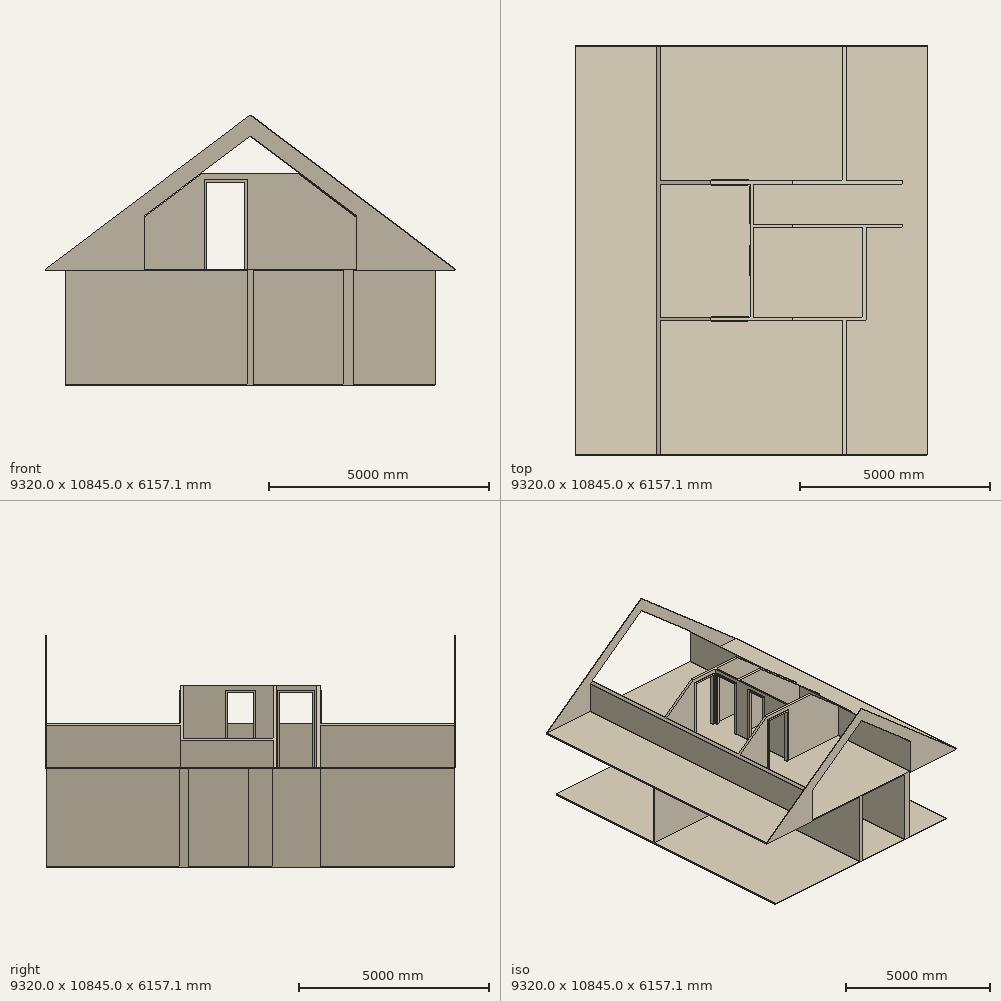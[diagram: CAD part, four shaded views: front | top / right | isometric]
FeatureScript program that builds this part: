
annotation { "Feature Type Name" : "Feature", "Feature Type Description" : "" }
export const myFeature = defineFeature(function(context is Context, id is Id, definition is map)
    precondition{}
    {
        {
            var Q0;
            Q0=qCreatedBy(makeId("Top.planeOp"),FACE);
            cPlane(context, id + "F0", {"entities" : qUnion([Q0]), "cplaneType" : CPlaneType.OFFSET, "offset" : 0 * mm, "width" : 150 * mm, "height" : 150 * mm});
        }
        {
            var Q0;
            Q0=qCreatedBy(makeId("Top.planeOp"),FACE);
            cPlane(context, id + "F1", {"entities" : qUnion([Q0]), "cplaneType" : CPlaneType.OFFSET, "offset" : 2600 * mm, "width" : 150 * mm, "height" : 150 * mm});
        }
        {
            var Q0;
            Q0=qCreatedBy(id+"F0.planeOp",FACE);
            var sketch = newSketch(context, id + "F2", { "sketchPlane" : qUnion([Q0])});
            skLineSegment(sketch, "E0.bottom", {"start": v(-4200, 0) * mm, "end": v(4200, 0) * mm});
            skLineSegment(sketch, "E0.top", {"start": v(-4200, 10795) * mm, "end": v(4200, 10795) * mm});
            skLineSegment(sketch, "E0.left", {"start": v(-4200, 10795) * mm, "end": v(-4200, 0) * mm});
            skLineSegment(sketch, "E0.right", {"start": v(4200, 10795) * mm, "end": v(4200, 0) * mm});
            skSolve(sketch);
        }
        {
            var Q0;
            Q0 = qSketchRegion(id + "F2", true);
            extrude(context, id + "F3", {"entities" : qUnion([Q0]), "oppositeDirection" : true, "depth" : 25 * mm, "offsetDistance" : 25 * mm});
        }
        {
            var Q0;
            Q0=makeQuery(id+"F3.opExtrude","CAP_FACE",FACE,{"disambiguationData":[OSD([sQuery(id+"F2.wireOp",EDGE,"E0.bottom"),sQuery(id+"F2.wireOp",EDGE,"E0.top"),sQuery(id+"F2.wireOp",EDGE,"E0.left"),sQuery(id+"F2.wireOp",EDGE,"E0.right")])],"isStart":true});
            var sketch = newSketch(context, id + "F4", { "sketchPlane" : qUnion([Q0])});
            skLineSegment(sketch, "E1", {"start": v(-66, 0) * mm, "end": v(-66, 5971.5) * mm});
            skLineSegment(sketch, "E2", {"start": v(-66, 0) * mm, "end": v(66, 0) * mm});
            skLineSegment(sketch, "E3", {"start": v(66, 0) * mm, "end": v(66, 3518.5) * mm});
            skLineSegment(sketch, "E4", {"start": v(2119, 0) * mm, "end": v(2349, 0) * mm});
            skLineSegment(sketch, "E5", {"start": v(2349, 0) * mm, "end": v(2349, 3518.5) * mm});
            skLineSegment(sketch, "E6", {"start": v(1066, 7175) * mm, "end": v(1066, 5975) * mm});
            skLineSegment(sketch, "E7", {"start": v(1066, 5975) * mm, "end": v(2900, 5975) * mm});
            skLineSegment(sketch, "E8", {"start": v(2900, 5975) * mm, "end": v(2900, 5355) * mm});
            skLineSegment(sketch, "E9", {"start": v(2900, 5355) * mm, "end": v(3000, 5355) * mm});
            skLineSegment(sketch, "E10", {"start": v(3000, 5355) * mm, "end": v(3000, 5975) * mm});
            skLineSegment(sketch, "E11", {"start": v(3000, 5975) * mm, "end": v(4200, 5975) * mm});
            skLineSegment(sketch, "E12", {"start": v(-66, 5971.5) * mm, "end": v(-4200, 5971.5) * mm});
            skLineSegment(sketch, "E13", {"start": v(-4200, 5971.5) * mm, "end": v(-4200, 6028.5) * mm});
            skLineSegment(sketch, "E14", {"start": v(-4200, 6028.5) * mm, "end": v(-66, 6028.5) * mm});
            skLineSegment(sketch, "E15", {"start": v(-66, 6028.5) * mm, "end": v(-66, 10800) * mm});
            skLineSegment(sketch, "E16", {"start": v(-66, 10800) * mm, "end": v(66, 10800) * mm});
            skLineSegment(sketch, "E17", {"start": v(2119, 0) * mm, "end": v(2119, 3518.5) * mm});
            skLineSegment(sketch, "E18", {"start": v(2119, 3518.5) * mm, "end": v(66, 3518.5) * mm});
            skLineSegment(sketch, "E19", {"start": v(2349, 3518.5) * mm, "end": v(4200, 3518.5) * mm});
            skLineSegment(sketch, "E20", {"start": v(4200, 3518.5) * mm, "end": v(4200, 3748.5) * mm});
            skLineSegment(sketch, "E21", {"start": v(4200, 3748.5) * mm, "end": v(66, 3748.5) * mm});
            skPoint(sketch, "E22", {"position": v(2234, 0) * mm});
            skPoint(sketch, "E23", {"position": v(4200, 3633.5) * mm});
            skPoint(sketch, "E24", {"position": v(-4200, 6000) * mm});
            skLineSegment(sketch, "E25", {"start": v(66, 3748.5) * mm, "end": v(66, 7175) * mm});
            skLineSegment(sketch, "E26", {"start": v(66, 10800) * mm, "end": v(66, 7242) * mm});
            skLineSegment(sketch, "E27", {"start": v(66, 7175) * mm, "end": v(1066, 7175) * mm});
            skLineSegment(sketch, "E28", {"start": v(66, 7242) * mm, "end": v(4200, 7242) * mm});
            skLineSegment(sketch, "E29", {"start": v(4200, 7242) * mm, "end": v(4200, 5975) * mm});
            skSolve(sketch);
        }
        {
            var Q0;
            Q0 = qSketchRegion(id + "F4", true);
            var Q1;
            Q1=qCreatedBy(id+"F1.planeOp",FACE);
            extrude(context, id + "F5", {"entities" : qUnion([Q0]), "operationType" : NewBodyOperationType.ADD, "endBound" : BoundingType.UP_TO_SURFACE, "depth" : 25 * mm, "endBoundEntityFace" : qUnion([Q1]), "offsetDistance" : 25 * mm});
        }
        {
            var Q0;
            Q0=qCreatedBy(id+"F1.planeOp",FACE);
            var sketch = newSketch(context, id + "F6", { "sketchPlane" : qUnion([Q0])});
            skLineSegment(sketch, "E30.bottom", {"start": v(-4660, 10795) * mm, "end": v(4660, 10795) * mm});
            skLineSegment(sketch, "E30.top", {"start": v(-4660, 0) * mm, "end": v(4660, 0) * mm});
            skLineSegment(sketch, "E30.left", {"start": v(-4660, 10795) * mm, "end": v(-4660, 0) * mm});
            skLineSegment(sketch, "E30.right", {"start": v(4660, 10795) * mm, "end": v(4660, 0) * mm});
            skSolve(sketch);
        }
        {
            var Q0;
            Q0 = qSketchRegion(id + "F6", true);
            extrude(context, id + "F7", {"entities" : qUnion([Q0]), "operationType" : NewBodyOperationType.ADD, "depth" : 25 * mm, "offsetDistance" : 25 * mm});
        }
        {
            var Q0;
            Q0=makeQuery(id+"F7.opExtrude","SWEPT_FACE",FACE,{"disambiguationData":[OSD([sQuery(id+"F6.wireOp",EDGE,"E30.bottom")])]});
            var sketch = newSketch(context, id + "F8", { "sketchPlane" : qUnion([Q0])});
            skLineSegment(sketch, "E31.top", {"start": v(-2415, 3833.53) * mm, "end": v(0, 5653.36) * mm});
            skLineSegment(sketch, "E31.left", {"start": v(-2415, 2600) * mm, "end": v(-2415, 3833.53) * mm});
            skLineSegment(sketch, "E32", {"start": v(-2415, 2600) * mm, "end": v(-4658.15, 2600) * mm});
            skLineSegment(sketch, "E33", {"start": v(-4658.15, 2600) * mm, "end": v(-4658.15, 2621.92) * mm});
            skLineSegment(sketch, "E34", {"start": v(-4658.15, 2621.92) * mm, "end": v(0, 6132.09) * mm});
            skLineSegment(sketch, "E35", {"start": v(0, 6132.09) * mm, "end": v(4658.15, 2621.92) * mm});
            skLineSegment(sketch, "E36", {"start": v(4658.15, 2621.92) * mm, "end": v(4658.15, 2600) * mm});
            skLineSegment(sketch, "E37", {"start": v(4658.15, 2600) * mm, "end": v(2415, 2600) * mm});
            skLineSegment(sketch, "E38", {"start": v(2415, 2600) * mm, "end": v(2415, 3833.53) * mm});
            skLineSegment(sketch, "E39", {"start": v(2415, 3833.53) * mm, "end": v(0, 5653.36) * mm});
            skSolve(sketch);
        }
        {
            var Q0;
            Q0 = qSketchRegion(id + "F8", true);
            extrude(context, id + "F9", {"entities" : qUnion([Q0]), "operationType" : NewBodyOperationType.ADD, "depth" : 25 * mm, "offsetDistance" : 25 * mm});
        }
        {
            var Q0;
            Q0=qCreatedBy(id+"F1.planeOp",FACE);
            var sketch = newSketch(context, id + "F10", { "sketchPlane" : qUnion([Q0])});
            skLineSegment(sketch, "E40", {"start": v(-2510, 10795) * mm, "end": v(-2510, 0) * mm});
            skLineSegment(sketch, "E41", {"start": v(-2510, 0) * mm, "end": v(-2415, 0) * mm});
            skLineSegment(sketch, "E42", {"start": v(-2415, 0) * mm, "end": v(-2415, 3535) * mm});
            skLineSegment(sketch, "E43", {"start": v(-2415, 3535) * mm, "end": v(2415, 3535) * mm});
            skLineSegment(sketch, "E44", {"start": v(2415, 3535) * mm, "end": v(2415, 0) * mm});
            skLineSegment(sketch, "E45", {"start": v(2415, 0) * mm, "end": v(2510, 0) * mm});
            skLineSegment(sketch, "E46", {"start": v(2510, 0) * mm, "end": v(2510, 3535) * mm});
            skLineSegment(sketch, "E47", {"start": v(2510, 3535) * mm, "end": v(3035, 3535) * mm});
            skLineSegment(sketch, "E48", {"start": v(3035, 3535) * mm, "end": v(3035, 5995) * mm});
            skLineSegment(sketch, "E49", {"start": v(3035, 5995) * mm, "end": v(4660, 5995) * mm});
            skLineSegment(sketch, "E50", {"start": v(4660, 5995) * mm, "end": v(4660, 6090) * mm});
            skLineSegment(sketch, "E51", {"start": v(4660, 6090) * mm, "end": v(40, 6090) * mm});
            skLineSegment(sketch, "E52", {"start": v(40, 6090) * mm, "end": v(40, 7150) * mm});
            skLineSegment(sketch, "E53", {"start": v(40, 7150) * mm, "end": v(4660, 7150) * mm});
            skLineSegment(sketch, "E54", {"start": v(4660, 7150) * mm, "end": v(4660, 7245) * mm});
            skLineSegment(sketch, "E55", {"start": v(4660, 7245) * mm, "end": v(2510, 7245) * mm});
            skLineSegment(sketch, "E56", {"start": v(2510, 7245) * mm, "end": v(2510, 10795) * mm});
            skLineSegment(sketch, "E57", {"start": v(2510, 10795) * mm, "end": v(2415, 10795) * mm});
            skLineSegment(sketch, "E58", {"start": v(2415, 10795) * mm, "end": v(2415, 7245) * mm});
            skLineSegment(sketch, "E59", {"start": v(2415, 7245) * mm, "end": v(-2415, 7245) * mm});
            skLineSegment(sketch, "E60", {"start": v(-2415, 7245) * mm, "end": v(-2415, 10795) * mm});
            skLineSegment(sketch, "E61", {"start": v(-2415, 10795) * mm, "end": v(-2510, 10795) * mm});
            skLineSegment(sketch, "E62.bottom", {"start": v(-2415, 7150) * mm, "end": v(-15, 7150) * mm});
            skLineSegment(sketch, "E62.top", {"start": v(-2415, 3630) * mm, "end": v(-15, 3630) * mm});
            skLineSegment(sketch, "E62.left", {"start": v(-2415, 7150) * mm, "end": v(-2415, 3630) * mm});
            skLineSegment(sketch, "E62.right", {"start": v(-15, 7150) * mm, "end": v(-15, 3630) * mm});
            skLineSegment(sketch, "E63.bottom", {"start": v(40, 5995) * mm, "end": v(2940, 5995) * mm});
            skLineSegment(sketch, "E63.top", {"start": v(40, 3630) * mm, "end": v(2940, 3630) * mm});
            skLineSegment(sketch, "E63.left", {"start": v(40, 5995) * mm, "end": v(40, 3630) * mm});
            skLineSegment(sketch, "E63.right", {"start": v(2940, 5995) * mm, "end": v(2940, 3630) * mm});
            skSolve(sketch);
        }
        {
            var Q0;
            Q0 = qSketchRegion(id + "F10", true);
            extrude(context, id + "F11", {"entities" : qUnion([Q0]), "operationType" : NewBodyOperationType.ADD, "depth" : 2200 * mm, "offsetDistance" : 25 * mm});
        }
        {
            var Q0;
            Q0=makeQuery(id+"F11.boolean.opBoolean","MERGE",FACE,{"derivedFrom":[makeQuery(id+"F7.opExtrude","SWEPT_FACE",FACE,{"disambiguationData":[OSD([sQuery(id+"F6.wireOp",EDGE,"E30.top")])]}),makeQuery(id+"F11.opExtrude","SWEPT_FACE",FACE,{"disambiguationData":[OSD([sQuery(id+"F10.wireOp",EDGE,"E41")])]}),makeQuery(id+"F11.opExtrude","SWEPT_FACE",FACE,{"disambiguationData":[OSD([sQuery(id+"F10.wireOp",EDGE,"E45")])]})]});
            var sketch = newSketch(context, id + "F12", { "sketchPlane" : qUnion([Q0])});
            skLineSegment(sketch, "E64.top", {"start": v(-2415, 3833.53) * mm, "end": v(0, 5653.36) * mm});
            skLineSegment(sketch, "E64.left", {"start": v(-2415, 2600) * mm, "end": v(-2415, 3833.53) * mm});
            skLineSegment(sketch, "E65", {"start": v(-2415, 2600) * mm, "end": v(-4658.15, 2600) * mm});
            skLineSegment(sketch, "E66", {"start": v(-4658.15, 2600) * mm, "end": v(-4658.15, 2621.92) * mm});
            skLineSegment(sketch, "E67", {"start": v(-4658.15, 2621.92) * mm, "end": v(0, 6132.09) * mm});
            skLineSegment(sketch, "E68", {"start": v(0, 6132.09) * mm, "end": v(4658.15, 2621.92) * mm});
            skLineSegment(sketch, "E69", {"start": v(4658.15, 2621.92) * mm, "end": v(4658.15, 2600) * mm});
            skLineSegment(sketch, "E70", {"start": v(4658.15, 2600) * mm, "end": v(2415, 2600) * mm});
            skLineSegment(sketch, "E71", {"start": v(2415, 2600) * mm, "end": v(2415, 3833.53) * mm});
            skLineSegment(sketch, "E72", {"start": v(2415, 3833.53) * mm, "end": v(0, 5653.36) * mm});
            skSolve(sketch);
        }
        {
            var Q0;
            Q0 = qSketchRegion(id + "F12", true);
            extrude(context, id + "F13", {"entities" : qUnion([Q0]), "operationType" : NewBodyOperationType.ADD, "depth" : 25 * mm, "offsetDistance" : 25 * mm});
        }
        {
            var Q0;
            Q0=makeQuery(id+"F11.opExtrude","SWEPT_FACE",FACE,{"disambiguationData":[OSD([sQuery(id+"F10.wireOp",EDGE,"E57")])]});
            var sketch = newSketch(context, id + "F14", { "sketchPlane" : qUnion([Q0])});
            skLineSegment(sketch, "E73", {"start": v(-4660, 4800) * mm, "end": v(-4660, 2625) * mm});
            skLineSegment(sketch, "E74", {"start": v(-3980.91, 2625) * mm, "end": v(-2415, 3805) * mm});
            skLineSegment(sketch, "E75", {"start": v(-1094.6, 4800) * mm, "end": v(-4660, 4800) * mm});
            skLineSegment(sketch, "E76", {"start": v(1094.6, 4800) * mm, "end": v(4660, 4800) * mm});
            skLineSegment(sketch, "E77", {"start": v(-4660, 2625) * mm, "end": v(-3980.91, 2625) * mm});
            skLineSegment(sketch, "E78", {"start": v(2415, 3805) * mm, "end": v(3980.91, 2625) * mm});
            skLineSegment(sketch, "E79", {"start": v(4660, 2625) * mm, "end": v(4660, 4800) * mm});
            skLineSegment(sketch, "E80", {"start": v(4660, 2625) * mm, "end": v(3980.91, 2625) * mm});
            skLineSegment(sketch, "E81", {"start": v(2415, 3805) * mm, "end": v(1094.6, 4800) * mm});
            skLineSegment(sketch, "E82", {"start": v(-2415, 3805) * mm, "end": v(-1094.6, 4800) * mm});
            skSolve(sketch);
        }
        {
            var Q0;
            Q0 = qSketchRegion(id + "F14", true);
            extrude(context, id + "F15", {"entities" : qUnion([Q0]), "operationType" : NewBodyOperationType.REMOVE, "oppositeDirection" : true, "depth" : 10795 * mm, "offsetDistance" : 25 * mm});
        }
        {
            var Q0;
            Q0=makeQuery(id+"F11.opExtrude","SWEPT_FACE",FACE,{"disambiguationData":[OSD([sQuery(id+"F10.wireOp",EDGE,"E59")])]});
            var sketch = newSketch(context, id + "F16", { "sketchPlane" : qUnion([Q0])});
            skLineSegment(sketch, "E83.bottom", {"start": v(135, 4605) * mm, "end": v(995, 4605) * mm});
            skLineSegment(sketch, "E83.top", {"start": v(135, 2625) * mm, "end": v(995, 2625) * mm});
            skLineSegment(sketch, "E83.left", {"start": v(135, 4605) * mm, "end": v(135, 2625) * mm});
            skLineSegment(sketch, "E83.right", {"start": v(995, 4605) * mm, "end": v(995, 2625) * mm});
            skSolve(sketch);
        }
        {
            var Q0;
            Q0 = qSketchRegion(id + "F16", true);
            var Q1;
            Q1=makeQuery(id+"F11.opExtrude","SWEPT_FACE",FACE,{"disambiguationData":[OSD([sQuery(id+"F10.wireOp",EDGE,"E43")])]});
            extrude(context, id + "F17", {"entities" : qUnion([Q0]), "operationType" : NewBodyOperationType.REMOVE, "endBound" : BoundingType.UP_TO_SURFACE, "oppositeDirection" : true, "depth" : 25 * mm, "endBoundEntityFace" : qUnion([Q1]), "offsetDistance" : 25 * mm});
        }
        {
            var Q0;
            Q0=makeQuery(id+"F11.opExtrude","SWEPT_FACE",FACE,{"disambiguationData":[OSD([sQuery(id+"F10.wireOp",EDGE,"E59")])]});
            var sketch = newSketch(context, id + "F18", { "sketchPlane" : qUnion([Q0])});
            skLineSegment(sketch, "E84", {"start": v(135, 2625) * mm, "end": v(75, 2625) * mm});
            skLineSegment(sketch, "E85", {"start": v(75, 2625) * mm, "end": v(75, 4665) * mm});
            skLineSegment(sketch, "E86", {"start": v(75, 4665) * mm, "end": v(1055, 4665) * mm});
            skLineSegment(sketch, "E87", {"start": v(1055, 4665) * mm, "end": v(1055, 2625) * mm});
            skLineSegment(sketch, "E88", {"start": v(1055, 2625) * mm, "end": v(995, 2625) * mm});
            skLineSegment(sketch, "E89", {"start": v(995, 2625) * mm, "end": v(995, 4605) * mm});
            skLineSegment(sketch, "E90", {"start": v(995, 4605) * mm, "end": v(135, 4605) * mm});
            skLineSegment(sketch, "E91", {"start": v(135, 4605) * mm, "end": v(135, 2625) * mm});
            skSolve(sketch);
        }
        {
            var Q0;
            Q0 = qSketchRegion(id + "F18", true);
            extrude(context, id + "F19", {"entities" : qUnion([Q0]), "operationType" : NewBodyOperationType.ADD, "depth" : 25 * mm, "offsetDistance" : 25 * mm, "hasSecondDirection" : true, "secondDirectionOppositeDirection" : true, "secondDirectionDepth" : 95 * mm + 25 * mm});
        }
        {
            var Q0;
            Q0=makeQuery(id+"F11.opExtrude","SWEPT_FACE",FACE,{"disambiguationData":[OSD([sQuery(id+"F10.wireOp",EDGE,"E43")])]});
            var sketch = newSketch(context, id + "F20", { "sketchPlane" : qUnion([Q0])});
            skLineSegment(sketch, "E92", {"start": v(-995, 2625) * mm, "end": v(-1055, 2625) * mm});
            skLineSegment(sketch, "E93", {"start": v(-1055, 2625) * mm, "end": v(-1055, 4665) * mm});
            skLineSegment(sketch, "E94", {"start": v(-1055, 4665) * mm, "end": v(-75, 4665) * mm});
            skLineSegment(sketch, "E95", {"start": v(-75, 4665) * mm, "end": v(-75, 2625) * mm});
            skLineSegment(sketch, "E96", {"start": v(-75, 2625) * mm, "end": v(-135, 2625) * mm});
            skLineSegment(sketch, "E97", {"start": v(-135, 2625) * mm, "end": v(-135, 4605) * mm});
            skLineSegment(sketch, "E98", {"start": v(-135, 4605) * mm, "end": v(-995, 4605) * mm});
            skLineSegment(sketch, "E99", {"start": v(-995, 4605) * mm, "end": v(-995, 2625) * mm});
            skSolve(sketch);
        }
        {
            var Q0;
            Q0 = qSketchRegion(id + "F20", true);
            extrude(context, id + "F21", {"entities" : qUnion([Q0]), "operationType" : NewBodyOperationType.ADD, "depth" : 25 * mm, "offsetDistance" : 25 * mm, "hasSecondDirection" : true, "secondDirectionOppositeDirection" : true, "secondDirectionDepth" : 120 * mm});
        }
        {
            var Q0;
            Q0=makeQuery(id+"F11.opExtrude","SWEPT_FACE",FACE,{"disambiguationData":[OSD([sQuery(id+"F10.wireOp",EDGE,"E62.right")])]});
            var sketch = newSketch(context, id + "F22", { "sketchPlane" : qUnion([Q0])});
            skLineSegment(sketch, "E100.bottom", {"start": v(-6170, 2625) * mm, "end": v(-7030, 2625) * mm});
            skLineSegment(sketch, "E100.top", {"start": v(-6170, 4605) * mm, "end": v(-7030, 4605) * mm});
            skLineSegment(sketch, "E100.left", {"start": v(-6170, 2625) * mm, "end": v(-6170, 4605) * mm});
            skLineSegment(sketch, "E100.right", {"start": v(-7030, 2625) * mm, "end": v(-7030, 4605) * mm});
            skLineSegment(sketch, "E101.bottom", {"start": v(-4800, 2625) * mm, "end": v(-5470, 2625) * mm});
            skLineSegment(sketch, "E101.top", {"start": v(-4800, 4605) * mm, "end": v(-5470, 4605) * mm});
            skLineSegment(sketch, "E101.left", {"start": v(-4800, 2625) * mm, "end": v(-4800, 4605) * mm});
            skLineSegment(sketch, "E101.right", {"start": v(-5470, 2625) * mm, "end": v(-5470, 4605) * mm});
            skSolve(sketch);
        }
        {
            var Q0;
            Q0 = qSketchRegion(id + "F22", true);
            extrude(context, id + "F23", {"entities" : qUnion([Q0]), "operationType" : NewBodyOperationType.REMOVE, "oppositeDirection" : true, "depth" : 60 * mm, "offsetDistance" : 25 * mm});
        }
        {
            var Q0;
            Q0=makeQuery(id+"F11.opExtrude","SWEPT_FACE",FACE,{"disambiguationData":[OSD([sQuery(id+"F10.wireOp",EDGE,"E62.right")])]});
            var sketch = newSketch(context, id + "F24", { "sketchPlane" : qUnion([Q0])});
            skLineSegment(sketch, "E102", {"start": v(-4800, 2625) * mm, "end": v(-4740, 2625) * mm});
            skLineSegment(sketch, "E103", {"start": v(-4740, 2625) * mm, "end": v(-4740, 4665) * mm});
            skLineSegment(sketch, "E104", {"start": v(-4740, 4665) * mm, "end": v(-5530, 4665) * mm});
            skLineSegment(sketch, "E105", {"start": v(-5530, 4665) * mm, "end": v(-5530, 2625) * mm});
            skLineSegment(sketch, "E106", {"start": v(-5530, 2625) * mm, "end": v(-5470, 2625) * mm});
            skLineSegment(sketch, "E107", {"start": v(-5470, 2625) * mm, "end": v(-5470, 4605) * mm});
            skLineSegment(sketch, "E108", {"start": v(-5470, 4605) * mm, "end": v(-4800, 4605) * mm});
            skLineSegment(sketch, "E109", {"start": v(-4800, 4605) * mm, "end": v(-4800, 2625) * mm});
            skLineSegment(sketch, "E110", {"start": v(-7030, 2625) * mm, "end": v(-7090, 2625) * mm});
            skLineSegment(sketch, "E111", {"start": v(-7090, 2625) * mm, "end": v(-7090, 4665) * mm});
            skLineSegment(sketch, "E112", {"start": v(-7090, 4665) * mm, "end": v(-6110, 4665) * mm});
            skLineSegment(sketch, "E113", {"start": v(-6110, 4665) * mm, "end": v(-6110, 2625) * mm});
            skLineSegment(sketch, "E114", {"start": v(-6110, 2625) * mm, "end": v(-6170, 2625) * mm});
            skLineSegment(sketch, "E115", {"start": v(-6170, 2625) * mm, "end": v(-6170, 4605) * mm});
            skLineSegment(sketch, "E116", {"start": v(-6170, 4605) * mm, "end": v(-7030, 4605) * mm});
            skLineSegment(sketch, "E117", {"start": v(-7030, 4605) * mm, "end": v(-7030, 2625) * mm});
            skSolve(sketch);
        }
        {
            var Q0;
            Q0 = qSketchRegion(id + "F24", true);
            extrude(context, id + "F25", {"entities" : qUnion([Q0]), "operationType" : NewBodyOperationType.ADD, "depth" : 25 * mm, "offsetDistance" : 25 * mm, "hasSecondDirection" : true, "secondDirectionOppositeDirection" : true, "secondDirectionDepth" : 55 * mm + 25 * mm});
        }
    });
